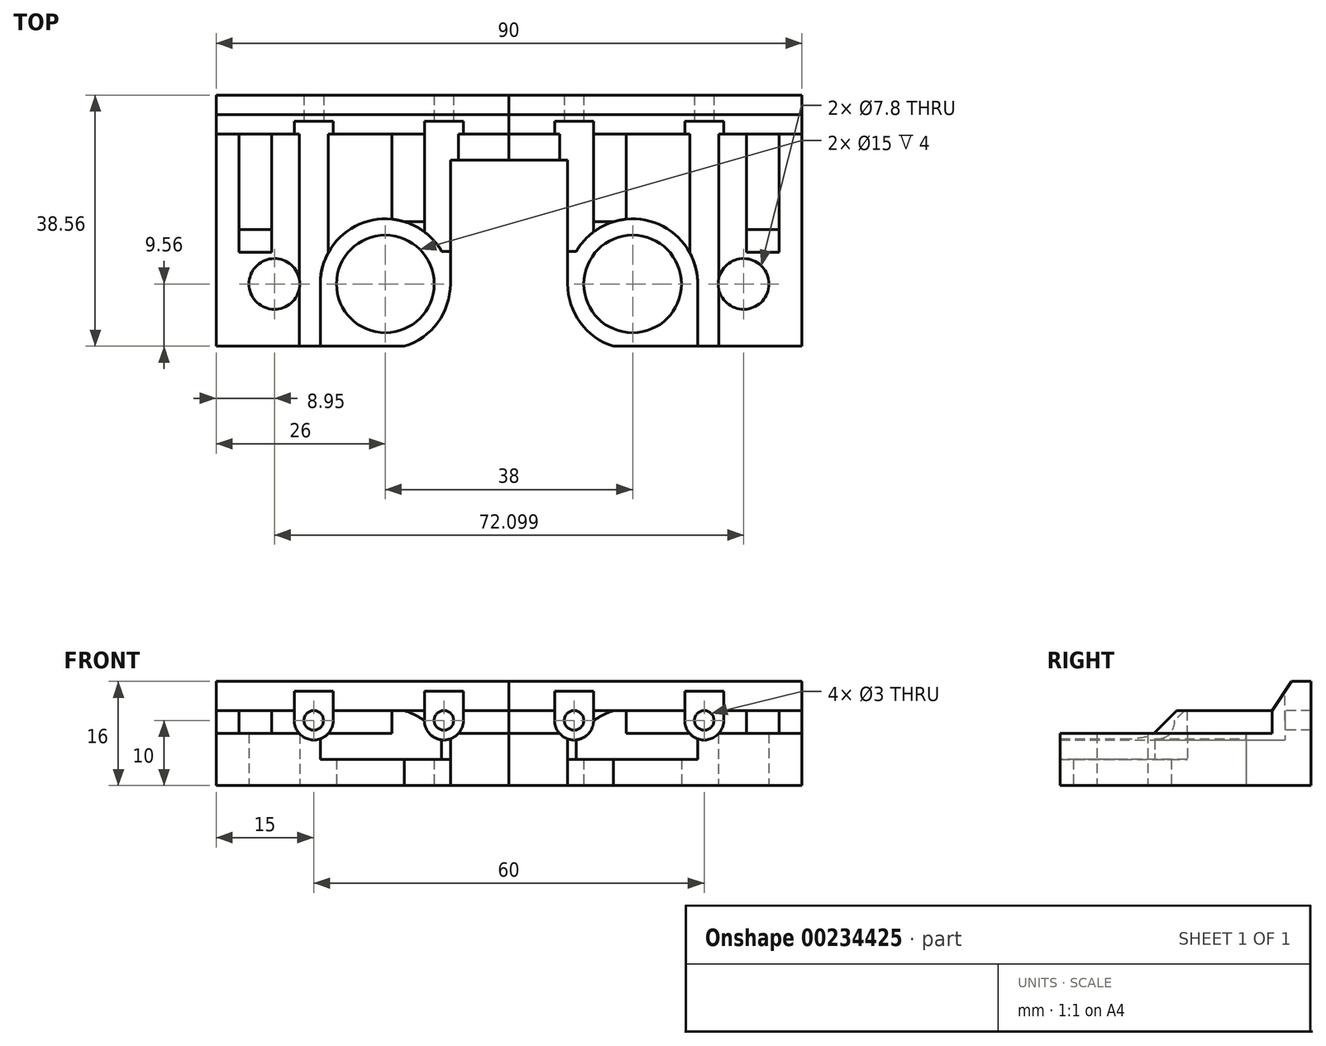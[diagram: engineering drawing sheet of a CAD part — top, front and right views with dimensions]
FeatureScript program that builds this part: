
annotation { "Feature Type Name" : "Feature", "Feature Type Description" : "" }
export const myFeature = defineFeature(function(context is Context, id is Id, definition is map)
    precondition{}
    {
        {
            var Q0;
            Q0=qCreatedBy(makeId("Top.planeOp"),FACE);
            var sketch = newSketch(context, id + "F0", { "sketchPlane" : qUnion([Q0])});
            skLineSegment(sketch, "E0", {"start": v(0, 0) * mm, "end": v(-45, 0) * mm});
            skCircle(sketch, "E1", {"center": v(-36.05, -29) * mm, "radius": 3.9 * mm});
            skLineSegment(sketch, "E2", {"start": v(0, 0) * mm, "end": v(0, -10) * mm});
            skLineSegment(sketch, "E3", {"start": v(0, -10) * mm, "end": v(-27, -10) * mm});
            skLineSegment(sketch, "E4", {"start": v(-45, 0) * mm, "end": v(-45, -25) * mm});
            skLineSegment(sketch, "E5", {"start": v(-27, -10) * mm, "end": v(-45, -10) * mm});
            skPoint(sketch, "E5.endSnap0", {"position": v(-45, -12.5) * mm});
            skLineSegment(sketch, "E6", {"start": v(-30.15, -29) * mm, "end": v(-30.15, -10) * mm});
            skLineSegment(sketch, "E7", {"start": v(-30.15, -38.56) * mm, "end": v(-45, -43.3) * mm});
            skLineSegment(sketch, "E8", {"start": v(-30.15, -29) * mm, "end": v(-30.15, -38.56) * mm});
            skLineSegment(sketch, "E9", {"start": v(-45, -25) * mm, "end": v(-45, -43.3) * mm});
            skCircle(sketch, "E10", {"center": v(-34.5, -13.5) * mm, "radius": 1.5 * mm});
            skCircle(sketch, "E11", {"center": v(-3.5, -13.5) * mm, "radius": 1.5 * mm});
            skCircle(sketch, "E12", {"center": v(-34.5, -44.5) * mm, "radius": 1.5 * mm});
            skLineSegment(sketch, "E13", {"start": v(-34.5, -13.5) * mm, "end": v(-3.5, -13.5) * mm, "construction": true});
            skLineSegment(sketch, "E14", {"start": v(-19, -13.5) * mm, "end": v(-19, -44.5) * mm, "construction": true});
            skCircle(sketch, "E15", {"center": v(-19, -29) * mm, "radius": 7.5 * mm});
            skArc(sketch, "E16", {"start": v(-16.06, -38.56) * mm, "mid": v(-19, -19) * mm, "end": v(-21.94, -38.56) * mm});
            skLineSegment(sketch, "E17", {"start": v(-9, -29) * mm, "end": v(-9, -10) * mm});
            skLineSegment(sketch, "E18", {"start": v(-30.15, -38.56) * mm, "end": v(-16.06, -38.56) * mm});
            skLineSegment(sketch, "E19", {"start": v(-24.44, -37.4) * mm, "end": v(-24.44, -38.56) * mm});
            skLineSegment(sketch, "E20", {"start": v(-9, -24) * mm, "end": v(-10.34, -24) * mm});
            skLineSegment(sketch, "E21", {"start": v(-45, -6) * mm, "end": v(0, -6) * mm});
            skLineSegment(sketch, "E22", {"start": v(-29, -29) * mm, "end": v(-29, -38.56) * mm});
            skLineSegment(sketch, "E23", {"start": v(-30.15, -38.56) * mm, "end": v(-45, -38.56) * mm});
            skSolve(sketch);
        }
        {
            var Q0;
            Q0=makeQuery(id+"F0.imprint","IMPRINT",FACE,{"disambiguationData":[TD([[makeQuery(id+"F0.imprint","IMPRINT",EDGE,{"derivedFrom":sQuery(id+"F0.wireOp",EDGE,"E1")}),-1.0]])]});
            var Q1;
            {var subQ1=sQuery(id+"F0.wireOp",EDGE,"E6");Q1=makeQuery(id+"F0.imprint","IMPRINT",FACE,{"disambiguationData":[TD([[makeQuery(id+"F0.imprint","IMPRINT",EDGE,{"derivedFrom":subQ1}),-1.0]])]});}
            var Q2;
            Q2=makeQuery(id+"F0.imprint","IMPRINT",FACE,{"disambiguationData":[TD([[makeQuery(id+"F0.imprint","IMPRINT",EDGE,{"derivedFrom":sQuery(id+"F0.wireOp",EDGE,"E10")}),1.0]])]});
            var Q3;
            {var subQ3=sQuery(id+"F0.wireOp",EDGE,"E21");Q3=makeQuery(id+"F0.imprint","IMPRINT",FACE,{"disambiguationData":[TD([[makeQuery(id+"F0.imprint","IMPRINT",EDGE,{"derivedFrom":subQ3}),-1.0]])]});}
            extrude(context, id + "F1", {"entities" : qUnion([Q0, Q1, Q2, Q3]), "depth" : 16 * mm});
        }
        {
            var Q0;
            {var subQ3=sQuery(id+"F0.wireOp",EDGE,"E19");Q0=makeQuery(id+"F0.imprint","IMPRINT",FACE,{"disambiguationData":[TD([[makeQuery(id+"F0.imprint","IMPRINT",EDGE,{"derivedFrom":subQ3}),1.0]])]});}
            var Q1;
            {var subQ3=sQuery(id+"F0.wireOp",EDGE,"E20");Q1=makeQuery(id+"F0.imprint","IMPRINT",FACE,{"disambiguationData":[TD([[makeQuery(id+"F0.imprint","IMPRINT",EDGE,{"derivedFrom":subQ3}),1.0]])]});}
            var Q2;
            Q2=makeQuery(id+"F0.imprint","IMPRINT",FACE,{"disambiguationData":[TD([[makeQuery(id+"F0.imprint","IMPRINT",EDGE,{"derivedFrom":sQuery(id+"F0.wireOp",EDGE,"E15")}),-1.0]])]});
            var Q3;
            {var subQ0=sQuery(id+"F0.wireOp",EDGE,"E19");Q3=makeQuery(id+"F0.imprint","IMPRINT",FACE,{"disambiguationData":[TD([[makeQuery(id+"F0.imprint","IMPRINT",EDGE,{"derivedFrom":subQ0}),-1.0]])]});}
            extrude(context, id + "F2", {"entities" : qUnion([Q0, Q1, Q2, Q3]), "operationType" : NewBodyOperationType.ADD, "depth" : 4 * mm});
        }
        {
            var Q0;
            Q0=makeQuery(id+"F1.opExtrude","SWEPT_FACE",FACE,{"disambiguationData":[OSD([sQuery(id+"F0.wireOp",EDGE,"E21")])]});
            var sketch = newSketch(context, id + "F3", { "sketchPlane" : qUnion([Q0])});
            skLineSegment(sketch, "E24", {"start": v(0, 10) * mm, "end": v(13, 10) * mm, "construction": true});
            skArc(sketch, "E25", {"start": v(7, 10) * mm, "mid": v(10, 7) * mm, "end": v(13, 10) * mm});
            skArc(sketch, "E26", {"start": v(27, 10) * mm, "mid": v(30, 7) * mm, "end": v(33, 10) * mm});
            skLineSegment(sketch, "E27", {"start": v(7, 10) * mm, "end": v(7, 16) * mm});
            skLineSegment(sketch, "E28", {"start": v(13, 10) * mm, "end": v(13, 16) * mm});
            skLineSegment(sketch, "E29", {"start": v(13, 16) * mm, "end": v(7, 16) * mm});
            skLineSegment(sketch, "E30", {"start": v(27, 10) * mm, "end": v(27, 16) * mm});
            skLineSegment(sketch, "E31", {"start": v(33, 10) * mm, "end": v(33, 16) * mm});
            skLineSegment(sketch, "E32", {"start": v(33, 16) * mm, "end": v(27, 16) * mm});
            skLineSegment(sketch, "E33", {"start": v(7, 10) * mm, "end": v(0, 10) * mm});
            skLineSegment(sketch, "E34", {"start": v(0, 16) * mm, "end": v(7, 16) * mm});
            skLineSegment(sketch, "E35", {"start": v(13, 13) * mm, "end": v(18, 13) * mm});
            skLineSegment(sketch, "E36", {"start": v(18, 13) * mm, "end": v(18, 10) * mm});
            skLineSegment(sketch, "E37", {"start": v(36.5, 13) * mm, "end": v(41.5, 13) * mm});
            skPoint(sketch, "E37.endSnap0", {"position": v(33, 13) * mm});
            skLineSegment(sketch, "E38", {"start": v(36.5, 13) * mm, "end": v(36.5, 10) * mm});
            skLineSegment(sketch, "E39", {"start": v(36.5, 10) * mm, "end": v(33, 10) * mm});
            skLineSegment(sketch, "E40", {"start": v(41.5, 13) * mm, "end": v(41.5, 10) * mm});
            skLineSegment(sketch, "E41", {"start": v(41.5, 10) * mm, "end": v(45, 10) * mm});
            skLineSegment(sketch, "E42", {"start": v(45, 16) * mm, "end": v(45, 10) * mm});
            skLineSegment(sketch, "E43", {"start": v(45, 16) * mm, "end": v(33, 16) * mm});
            skLineSegment(sketch, "E44", {"start": v(13, 16) * mm, "end": v(27, 16) * mm});
            skLineSegment(sketch, "E45", {"start": v(18, 10) * mm, "end": v(27, 10) * mm});
            skLineSegment(sketch, "E46.trimOffspring", {"start": v(18, 10) * mm, "end": v(45, 10) * mm, "construction": true});
            skLineSegment(sketch, "E47", {"start": v(0, 8) * mm, "end": v(7.76, 8) * mm});
            skLineSegment(sketch, "E48.trimOffspring", {"start": v(12.24, 8) * mm, "end": v(27.76, 8) * mm});
            skLineSegment(sketch, "E49.trimOffspring", {"start": v(32.24, 8) * mm, "end": v(45, 8) * mm});
            skLineSegment(sketch, "E50", {"start": v(18, 10) * mm, "end": v(18, 8) * mm});
            skLineSegment(sketch, "E51", {"start": v(36.5, 10) * mm, "end": v(36.5, 8) * mm});
            skLineSegment(sketch, "E52", {"start": v(41.5, 10) * mm, "end": v(41.5, 8) * mm});
            skLineSegment(sketch, "E53", {"start": v(13, 11.5) * mm, "end": v(18, 11.5) * mm});
            skLineSegment(sketch, "E54", {"start": v(36.5, 11.5) * mm, "end": v(41.5, 11.5) * mm});
            skCircle(sketch, "E55", {"center": v(10, 10) * mm, "radius": 1.5 * mm});
            skCircle(sketch, "E56", {"center": v(30, 10) * mm, "radius": 1.5 * mm});
            skSolve(sketch);
        }
        {
            var Q0;
            Q0=makeQuery(id+"F3.imprint","IMPRINT",FACE,{"disambiguationData":[TD([[makeQuery(id+"F3.imprint","IMPRINT",EDGE,{"derivedFrom":sQuery(id+"F3.wireOp",EDGE,"E27")}),1.0]])]});
            var Q1;
            {var subQ0=sQuery(id+"F3.wireOp",EDGE,"E27");Q1=makeQuery(id+"F3.imprint","IMPRINT",FACE,{"disambiguationData":[TD([[makeQuery(id+"F3.imprint","IMPRINT",EDGE,{"derivedFrom":subQ0}),-1.0]])]});}
            var Q2;
            {var subQ0=sQuery(id+"F3.wireOp",EDGE,"E33");Q2=makeQuery(id+"F3.imprint","IMPRINT",FACE,{"disambiguationData":[TD([[makeQuery(id+"F3.imprint","IMPRINT",EDGE,{"derivedFrom":subQ0}),1.0]])]});}
            var Q3;
            Q3=makeQuery(id+"F3.imprint","IMPRINT",FACE,{"disambiguationData":[TD([[makeQuery(id+"F3.imprint","IMPRINT",EDGE,{"derivedFrom":sQuery(id+"F3.wireOp",EDGE,"E30")}),1.0]])]});
            var Q4;
            {var subQ0=sQuery(id+"F3.wireOp",EDGE,"E45");Q4=makeQuery(id+"F3.imprint","IMPRINT",FACE,{"disambiguationData":[TD([[makeQuery(id+"F3.imprint","IMPRINT",EDGE,{"derivedFrom":subQ0}),-1.0]])]});}
            var Q5;
            Q5=makeQuery(id+"F3.imprint","IMPRINT",FACE,{"disambiguationData":[TD([[makeQuery(id+"F3.imprint","IMPRINT",EDGE,{"derivedFrom":sQuery(id+"F3.wireOp",EDGE,"E31")}),-1.0]])]});
            var Q6;
            {var subQ0=sQuery(id+"F3.wireOp",EDGE,"E39");Q6=makeQuery(id+"F3.imprint","IMPRINT",FACE,{"disambiguationData":[TD([[makeQuery(id+"F3.imprint","IMPRINT",EDGE,{"derivedFrom":subQ0}),1.0]])]});}
            var Q7;
            {var subQ0=sQuery(id+"F3.wireOp",EDGE,"E41");Q7=makeQuery(id+"F3.imprint","IMPRINT",FACE,{"disambiguationData":[TD([[makeQuery(id+"F3.imprint","IMPRINT",EDGE,{"derivedFrom":subQ0}),-1.0]])]});}
            var Q8;
            {var subQ0=sQuery(id+"F3.wireOp",EDGE,"E30");Q8=makeQuery(id+"F3.imprint","IMPRINT",FACE,{"disambiguationData":[TD([[makeQuery(id+"F3.imprint","IMPRINT",EDGE,{"derivedFrom":subQ0}),-1.0]])]});}
            var Q9;
            {var subQ0=sQuery(id+"F3.wireOp",EDGE,"E35");Q9=makeQuery(id+"F3.imprint","IMPRINT",FACE,{"disambiguationData":[TD([[makeQuery(id+"F3.imprint","IMPRINT",EDGE,{"derivedFrom":subQ0}),-1.0]])]});}
            var Q10;
            {var subQ0=sQuery(id+"F3.wireOp",EDGE,"E37");Q10=makeQuery(id+"F3.imprint","IMPRINT",FACE,{"disambiguationData":[TD([[makeQuery(id+"F3.imprint","IMPRINT",EDGE,{"derivedFrom":subQ0}),-1.0]])]});}
            var Q11;
            Q11=makeQuery(id+"F3.imprint","IMPRINT",FACE,{"disambiguationData":[TD([[makeQuery(id+"F3.imprint","IMPRINT",EDGE,{"derivedFrom":sQuery(id+"F3.wireOp",EDGE,"E55")}),1.0]])]});
            var Q12;
            Q12=makeQuery(id+"F3.imprint","IMPRINT",FACE,{"disambiguationData":[TD([[makeQuery(id+"F3.imprint","IMPRINT",EDGE,{"derivedFrom":sQuery(id+"F3.wireOp",EDGE,"E56")}),1.0]])]});
            extrude(context, id + "F4", {"entities" : qUnion([Q0, Q1, Q2, Q3, Q4, Q5, Q6, Q7, Q8, Q9, Q10, Q11, Q12]), "operationType" : NewBodyOperationType.REMOVE, "oppositeDirection" : true, "depth" : 50 * mm});
        }
        {
            var Q0;
            {var subQ1=sQuery(id+"F3.wireOp",EDGE,"E51");Q0=makeQuery(id+"F4.boolean.opBoolean","COPY",FACE,{"disambiguationData":[TD([makeQuery(id+"F1.opExtrude","SWEPT_FACE",FACE,{"disambiguationData":[OSD([sQuery(id+"F0.wireOp",EDGE,"E21")])]})])],"derivedFrom":makeQuery(id+"F4.opExtrude","SWEPT_FACE",FACE,{"disambiguationData":[OSD([sQuery(id+"F3.wireOp",EDGE,"E38"),subQ1])]})});}
            var sketch = newSketch(context, id + "F5", { "sketchPlane" : qUnion([Q0])});
            skLineSegment(sketch, "E57", {"start": v(-24.13, 8) * mm, "end": v(-20.63, 11.5) * mm});
            skLineSegment(sketch, "E58", {"start": v(-20.63, 11.5) * mm, "end": v(-26.63, 11.5) * mm});
            skLineSegment(sketch, "E59", {"start": v(-25.13, 8) * mm, "end": v(-24.13, 8) * mm});
            skLineSegment(sketch, "E60", {"start": v(-26.63, 11.5) * mm, "end": v(-42.02, 11.5) * mm});
            skLineSegment(sketch, "E61", {"start": v(-42.02, 11.5) * mm, "end": v(-42.02, 8) * mm});
            skLineSegment(sketch, "E62", {"start": v(-42.02, 8) * mm, "end": v(-25.13, 8) * mm});
            skSolve(sketch);
        }
        {
            var Q0;
            Q0=makeQuery(id+"F4.boolean.opBoolean","COPY",FACE,{"derivedFrom":makeQuery(id+"F4.opExtrude","SWEPT_FACE",FACE,{"disambiguationData":[OSD([sQuery(id+"F3.wireOp",EDGE,"E28")])]})});
            var sketch = newSketch(context, id + "F6", { "sketchPlane" : qUnion([Q0])});
            skLineSegment(sketch, "E63", {"start": v(-22.95, 8) * mm, "end": v(-19.45, 11.5) * mm});
            skLineSegment(sketch, "E64", {"start": v(-19.45, 11.5) * mm, "end": v(-27.34, 11.5) * mm});
            skLineSegment(sketch, "E65", {"start": v(-27.34, 11.5) * mm, "end": v(-27.34, 8) * mm});
            skLineSegment(sketch, "E66", {"start": v(-27.34, 8) * mm, "end": v(-22.95, 8) * mm});
            skSolve(sketch);
        }
        {
            var Q0;
            {var subQ0=sQuery(id+"F5.wireOp",EDGE,"E60");Q0=makeQuery(id+"F5.imprint","IMPRINT",FACE,{"disambiguationData":[TD([[makeQuery(id+"F5.imprint","IMPRINT",EDGE,{"derivedFrom":subQ0}),1.0]])]});}
            var Q1;
            {var subQ0=sQuery(id+"F5.wireOp",EDGE,"E57");Q1=makeQuery(id+"F5.imprint","IMPRINT",FACE,{"disambiguationData":[TD([[makeQuery(id+"F5.imprint","IMPRINT",EDGE,{"derivedFrom":subQ0}),1.0]])]});}
            var Q2;
            {var subQ2=sQuery(id+"F3.wireOp",EDGE,"E28");var subQ6=makeQuery(id+"F4.boolean.opBoolean","INTERSECT",EDGE,{"derivedFrom":[makeQuery(id+"F1.opExtrude","SWEPT_FACE",FACE,{"disambiguationData":[OSD([sQuery(id+"F0.wireOp",EDGE,"E16")])]}),makeQuery(id+"F4.opExtrude","SWEPT_FACE",FACE,{"disambiguationData":[OSD([subQ2])]})]});Q2=makeQuery(id+"F6.imprint","IMPRINT",FACE,{"disambiguationData":[TD([[makeQuery(id+"F6.imprint","IMPRINT",EDGE,{"derivedFrom":subQ6}),1.0]])]});}
            var Q3;
            {var subQ7=sQuery(id+"F6.wireOp",EDGE,"E65");Q3=makeQuery(id+"F6.imprint","IMPRINT",FACE,{"disambiguationData":[TD([[makeQuery(id+"F6.imprint","IMPRINT",EDGE,{"derivedFrom":subQ7}),1.0]])]});}
            extrude(context, id + "F7", {"entities" : qUnion([Q0, Q1, Q2, Q3]), "operationType" : NewBodyOperationType.REMOVE, "oppositeDirection" : true, "depth" : 5 * mm, "hasSecondDirection" : true, "secondDirectionOppositeDirection" : false, "secondDirectionDepth" : 1 * mm});
        }
        {
            var Q0;
            {var subQ0=sQuery(id+"F0.wireOp",EDGE,"E0");Q0=makeQuery(id+"F0.imprint","IMPRINT",FACE,{"disambiguationData":[TD([[makeQuery(id+"F0.imprint","IMPRINT",EDGE,{"derivedFrom":subQ0}),1.0]])]});}
            extrude(context, id + "F8", {"entities" : qUnion([Q0]), "operationType" : NewBodyOperationType.ADD, "depth" : 16 * mm});
        }
        {
            var Q0;
            {var subQ3=sQuery(id+"F3.wireOp",EDGE,"E30");Q0=makeQuery(id+"F3.imprint","IMPRINT",FACE,{"disambiguationData":[TD([[makeQuery(id+"F3.imprint","IMPRINT",EDGE,{"derivedFrom":subQ3}),-1.0]])]});}
            var Q1;
            {var subQ0=sQuery(id+"F3.wireOp",EDGE,"E27");Q1=makeQuery(id+"F3.imprint","IMPRINT",FACE,{"disambiguationData":[TD([[makeQuery(id+"F3.imprint","IMPRINT",EDGE,{"derivedFrom":subQ0}),-1.0]])]});}
            extrude(context, id + "F9", {"entities" : qUnion([Q0, Q1]), "operationType" : NewBodyOperationType.REMOVE, "depth" : 2 * mm});
        }
        {
            var Q0;
            Q0=makeQuery(id+"F3.imprint","IMPRINT",FACE,{"disambiguationData":[TD([[makeQuery(id+"F3.imprint","IMPRINT",EDGE,{"derivedFrom":sQuery(id+"F3.wireOp",EDGE,"E56")}),1.0]])]});
            var Q1;
            Q1=makeQuery(id+"F3.imprint","IMPRINT",FACE,{"disambiguationData":[TD([[makeQuery(id+"F3.imprint","IMPRINT",EDGE,{"derivedFrom":sQuery(id+"F3.wireOp",EDGE,"E55")}),1.0]])]});
            extrude(context, id + "F10", {"entities" : qUnion([Q0, Q1]), "operationType" : NewBodyOperationType.REMOVE, "depth" : 25 * mm});
        }
        {
            var Q0;
            {var subQ0=sQuery(id+"F0.wireOp",EDGE,"E4");Q0=makeQuery(id+"F8.boolean.opBoolean","MERGE",FACE,{"derivedFrom":[makeQuery(id+"F1.opExtrude","SWEPT_FACE",FACE,{"disambiguationData":[OSD([subQ0,sQuery(id+"F0.wireOp",EDGE,"E9")])]}),makeQuery(id+"F8.opExtrude","SWEPT_FACE",FACE,{"disambiguationData":[OSD([subQ0])]})]});}
            var sketch = newSketch(context, id + "F11", { "sketchPlane" : qUnion([Q0])});
            skLineSegment(sketch, "E67", {"start": v(3, 16) * mm, "end": v(6, 11.5) * mm});
            skLineSegment(sketch, "E68", {"start": v(6, 11.5) * mm, "end": v(6, 16) * mm});
            skLineSegment(sketch, "E69", {"start": v(6, 16) * mm, "end": v(3, 16) * mm});
            skSolve(sketch);
        }
        {
            var Q0;
            Q0=makeQuery(id+"F11.imprint","IMPRINT",FACE,{"disambiguationData":[TD([[makeQuery(id+"F11.imprint","IMPRINT",EDGE,{"derivedFrom":sQuery(id+"F11.wireOp",EDGE,"E67")}),1.0]])]});
            extrude(context, id + "F12", {"entities" : qUnion([Q0]), "operationType" : NewBodyOperationType.REMOVE, "oppositeDirection" : true, "depth" : 50 * mm});
        }
        {
            var Q0;
            Q0=makeQuery(id+"F1.opExtrude","SWEPT_BODY",BODY,{"disambiguationData":[OSD([sQuery(id+"F0.wireOp",EDGE,"E1"),sQuery(id+"F0.wireOp",EDGE,"E2"),sQuery(id+"F0.wireOp",EDGE,"E3"),sQuery(id+"F0.wireOp",EDGE,"E4"),sQuery(id+"F0.wireOp",EDGE,"E7"),sQuery(id+"F0.wireOp",EDGE,"E9"),sQuery(id+"F0.wireOp",EDGE,"E16"),sQuery(id+"F0.wireOp",EDGE,"E17"),sQuery(id+"F0.wireOp",EDGE,"E18"),sQuery(id+"F0.wireOp",EDGE,"E20"),sQuery(id+"F0.wireOp",EDGE,"E21"),sQuery(id+"F0.wireOp",EDGE,"E22")])]});
            var Q1;
            {var subQ0=sQuery(id+"F0.wireOp",EDGE,"E2");Q1=makeQuery(id+"F8.boolean.opBoolean","MERGE",FACE,{"derivedFrom":[makeQuery(id+"F1.opExtrude","SWEPT_FACE",FACE,{"disambiguationData":[OSD([subQ0])]}),makeQuery(id+"F8.opExtrude","SWEPT_FACE",FACE,{"disambiguationData":[OSD([subQ0])]})]});}
            mirror(context, id + "F13", {"entities" : qUnion([Q0]), "mirrorPlane" : qUnion([Q1])});
        }
    });
